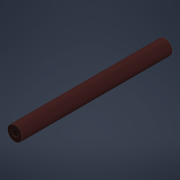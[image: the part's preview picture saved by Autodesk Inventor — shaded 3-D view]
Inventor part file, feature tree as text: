
AUTODESK INVENTOR PART (.ipt)
format: ipt  version: 2022 (Build 260153000, 153)  size: 111,104 bytes
history: native  units: mm
features: extrude x2, sketch x2
ambient origin geometry x8: Origin, YZ Plane, XZ Plane, XY Plane, X Axis, Y Axis, Z Axis, Center Point
bodies: Solid1 (feature_tree)
feature tree (4):
  extrude  "Extrusion1"  Depth=4200.0mm TaperAngle=0.0deg
  extrude  "Extrusion2"  Depth=10.0mm TaperAngle=0.0deg
  sketch  "Sketch1"  dims[d0=406.0mm d1=4200.0mm d2=0.0mm]
  sketch  "Sketch3"  dims[d3=175.0mm d4=10.0mm d5=0.0mm]
